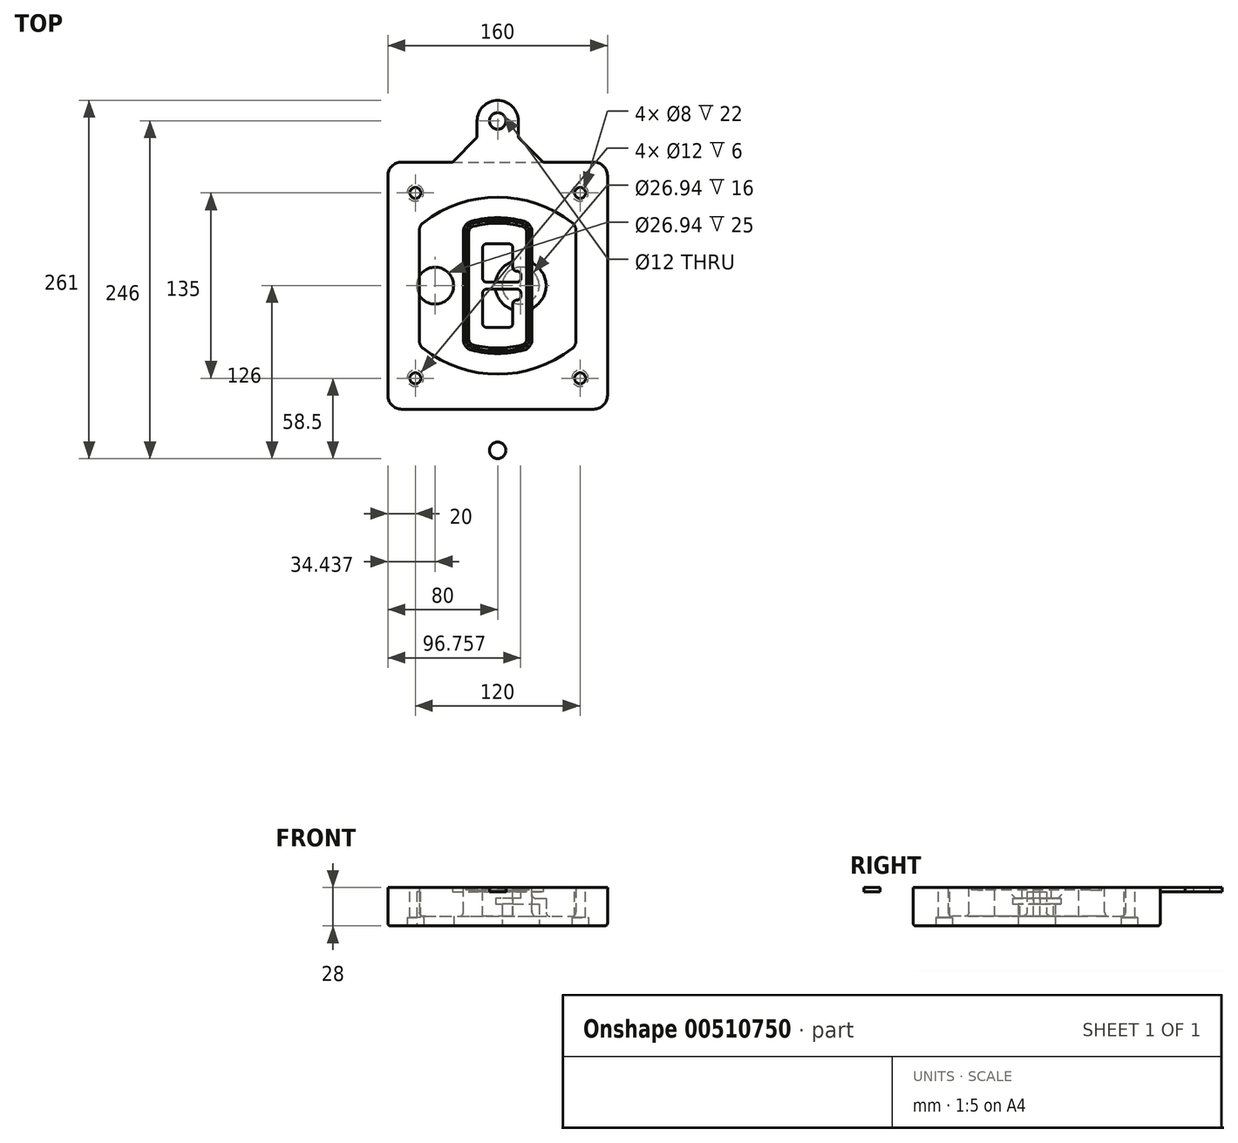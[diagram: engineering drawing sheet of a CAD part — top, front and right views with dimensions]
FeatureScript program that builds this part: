
annotation { "Feature Type Name" : "Feature", "Feature Type Description" : "" }
export const myFeature = defineFeature(function(context is Context, id is Id, definition is map)
    precondition{}
    {
        {
            var Q0;
            Q0=qCreatedBy(makeId("Top.planeOp"),FACE);
            var sketch = newSketch(context, id + "F0", { "sketchPlane" : qUnion([Q0])});
            skPoint(sketch, "E0.rect.middle", {"position": v(0, 0) * mm});
            skLineSegment(sketch, "E1.bottom", {"start": v(-70, -90) * mm, "end": v(70, -90) * mm});
            skLineSegment(sketch, "E1.top", {"start": v(-70, 90) * mm, "end": v(70, 90) * mm});
            skLineSegment(sketch, "E1.left", {"start": v(-80, -80) * mm, "end": v(-80, 80) * mm});
            skLineSegment(sketch, "E1.right", {"start": v(80, -80) * mm, "end": v(80, 80) * mm});
            skLineSegment(sketch, "E2", {"start": v(-80, 90) * mm, "end": v(80, -90) * mm, "construction": true});
            skLineSegment(sketch, "E3", {"start": v(80, 90) * mm, "end": v(-80, -90) * mm, "construction": true});
            skCircle(sketch, "E4", {"center": v(-60, 67.5) * mm, "radius": 4 * mm});
            skCircle(sketch, "E5", {"center": v(60, 67.5) * mm, "radius": 4 * mm});
            skCircle(sketch, "E6", {"center": v(60, -67.5) * mm, "radius": 4 * mm});
            skCircle(sketch, "E7", {"center": v(-60, -67.5) * mm, "radius": 4 * mm});
            skLineSegment(sketch, "E8", {"start": v(-60, 67.5) * mm, "end": v(60, 67.5) * mm, "construction": true});
            skLineSegment(sketch, "E9", {"start": v(60, 67.5) * mm, "end": v(60, -67.5) * mm, "construction": true});
            skLineSegment(sketch, "E10", {"start": v(60, -67.5) * mm, "end": v(-60, -67.5) * mm, "construction": true});
            skLineSegment(sketch, "E11", {"start": v(-60, -67.5) * mm, "end": v(-60, 67.5) * mm, "construction": true});
            skLineSegment(sketch, "E12", {"start": v(-60, 40.3) * mm, "end": v(-60, -40.3) * mm});
            skLineSegment(sketch, "E13", {"start": v(60, 40.3) * mm, "end": v(60, -40.3) * mm});
            skArc(sketch, "E14", {"start": v(56.15, 48.18) * mm, "mid": v(0, 67.5) * mm, "end": v(-56.15, 48.18) * mm});
            skArc(sketch, "E15", {"start": v(-56.15, -48.18) * mm, "mid": v(0, -67.5) * mm, "end": v(56.15, -48.18) * mm});
            skLineSegment(sketch, "E16", {"start": v(-60, 0) * mm, "end": v(60, 0) * mm, "construction": true});
            skPoint(sketch, "E17.visualSharp", {"position": v(-60, -45) * mm});
            skArc(sketch, "E17.filletArc", {"start": v(-60, -40.3) * mm, "mid": v(-58.99, -44.68) * mm, "end": v(-56.15, -48.18) * mm});
            skPoint(sketch, "E18.visualSharp", {"position": v(-60, 45) * mm});
            skArc(sketch, "E18.filletArc", {"start": v(-56.15, 48.18) * mm, "mid": v(-58.99, 44.68) * mm, "end": v(-60, 40.3) * mm});
            skPoint(sketch, "E19.visualSharp", {"position": v(60, 45) * mm});
            skArc(sketch, "E19.filletArc", {"start": v(60, 40.3) * mm, "mid": v(58.99, 44.68) * mm, "end": v(56.15, 48.18) * mm});
            skPoint(sketch, "E20.visualSharp", {"position": v(60, -45) * mm});
            skArc(sketch, "E20.filletArc", {"start": v(56.15, -48.18) * mm, "mid": v(58.99, -44.68) * mm, "end": v(60, -40.3) * mm});
            skPoint(sketch, "E21.visualSharp", {"position": v(-80, 90) * mm});
            skArc(sketch, "E21.filletArc", {"start": v(-70, 90) * mm, "mid": v(-77.07, 87.07) * mm, "end": v(-80, 80) * mm});
            skPoint(sketch, "E22.visualSharp", {"position": v(80, 90) * mm});
            skArc(sketch, "E22.filletArc", {"start": v(80, 80) * mm, "mid": v(77.07, 87.07) * mm, "end": v(70, 90) * mm});
            skPoint(sketch, "E23.visualSharp", {"position": v(80, -90) * mm});
            skArc(sketch, "E23.filletArc", {"start": v(70, -90) * mm, "mid": v(77.07, -87.07) * mm, "end": v(80, -80) * mm});
            skPoint(sketch, "E24.visualSharp", {"position": v(-80, -90) * mm});
            skArc(sketch, "E24.filletArc", {"start": v(-80, -80) * mm, "mid": v(-77.07, -87.07) * mm, "end": v(-70, -90) * mm});
            skArc(sketch, "E25.0", {"start": v(57, 40.3) * mm, "mid": v(56.3, 43.36) * mm, "end": v(54.3, 45.81) * mm});
            skLineSegment(sketch, "E25.1", {"start": v(57, 40.3) * mm, "end": v(57, -40.3) * mm});
            skArc(sketch, "E25.2", {"start": v(54.3, -45.81) * mm, "mid": v(56.3, -43.36) * mm, "end": v(57, -40.3) * mm});
            skArc(sketch, "E25.3", {"start": v(-54.3, -45.81) * mm, "mid": v(0, -64.5) * mm, "end": v(54.3, -45.81) * mm});
            skArc(sketch, "E25.4", {"start": v(-57, -40.3) * mm, "mid": v(-56.3, -43.36) * mm, "end": v(-54.3, -45.81) * mm});
            skArc(sketch, "E25.5", {"start": v(54.3, 45.81) * mm, "mid": v(0, 64.5) * mm, "end": v(-54.3, 45.81) * mm});
            skLineSegment(sketch, "E25.6", {"start": v(-57, 40.3) * mm, "end": v(-57, -40.3) * mm});
            skArc(sketch, "E25.7", {"start": v(-54.3, 45.81) * mm, "mid": v(-56.3, 43.36) * mm, "end": v(-57, 40.3) * mm});
            skArc(sketch, "E26.0", {"start": v(-58.62, 51.33) * mm, "mid": v(-62.58, 46.43) * mm, "end": v(-64, 40.3) * mm});
            skArc(sketch, "E26.1", {"start": v(58.62, 51.33) * mm, "mid": v(0, 71.5) * mm, "end": v(-58.62, 51.33) * mm});
            skArc(sketch, "E26.2", {"start": v(64, 40.3) * mm, "mid": v(62.58, 46.43) * mm, "end": v(58.62, 51.33) * mm});
            skLineSegment(sketch, "E26.3", {"start": v(64, 40.3) * mm, "end": v(64, -40.3) * mm});
            skArc(sketch, "E26.4", {"start": v(58.62, -51.33) * mm, "mid": v(62.58, -46.43) * mm, "end": v(64, -40.3) * mm});
            skLineSegment(sketch, "E26.5", {"start": v(-64, 40.3) * mm, "end": v(-64, -40.3) * mm});
            skArc(sketch, "E26.6", {"start": v(-58.62, -51.33) * mm, "mid": v(0, -71.5) * mm, "end": v(58.62, -51.33) * mm});
            skArc(sketch, "E26.7", {"start": v(-64, -40.3) * mm, "mid": v(-62.58, -46.43) * mm, "end": v(-58.62, -51.33) * mm});
            skSolve(sketch);
        }
        {
            var Q0;
            Q0=makeQuery(id+"F0.imprint","IMPRINT",FACE,{"disambiguationData":[TD([[makeQuery(id+"F0.imprint","IMPRINT",EDGE,{"derivedFrom":sQuery(id+"F0.wireOp",EDGE,"E1.bottom")}),1.0]])]});
            var Q1;
            Q1=makeQuery(id+"F0.imprint","IMPRINT",FACE,{"disambiguationData":[TD([[makeQuery(id+"F0.imprint","IMPRINT",EDGE,{"derivedFrom":sQuery(id+"F0.wireOp",EDGE,"E12")}),1.0]])]});
            var Q2;
            Q2=makeQuery(id+"F0.imprint","IMPRINT",FACE,{"disambiguationData":[TD([[makeQuery(id+"F0.imprint","IMPRINT",EDGE,{"derivedFrom":sQuery(id+"F0.wireOp",EDGE,"E25.0")}),1.0]])]});
            var Q3;
            Q3=makeQuery(id+"F0.imprint","IMPRINT",FACE,{"disambiguationData":[TD([[makeQuery(id+"F0.imprint","IMPRINT",EDGE,{"derivedFrom":sQuery(id+"F0.wireOp",EDGE,"E12")}),-1.0]])]});
            extrude(context, id + "F1", {"entities" : qUnion([Q0, Q1, Q2, Q3]), "oppositeDirection" : true, "depth" : 25 * mm});
        }
        {
            var Q0;
            Q0=makeQuery(id+"F0.imprint","IMPRINT",FACE,{"disambiguationData":[TD([[makeQuery(id+"F0.imprint","IMPRINT",EDGE,{"derivedFrom":sQuery(id+"F0.wireOp",EDGE,"E12")}),1.0]])]});
            extrude(context, id + "F2", {"entities" : qUnion([Q0]), "operationType" : NewBodyOperationType.ADD, "depth" : 3 * mm});
        }
        {
            var Q0;
            Q0=makeQuery(id+"F0.imprint","IMPRINT",FACE,{"disambiguationData":[TD([[makeQuery(id+"F0.imprint","IMPRINT",EDGE,{"derivedFrom":sQuery(id+"F0.wireOp",EDGE,"E25.0")}),1.0]])]});
            extrude(context, id + "F3", {"entities" : qUnion([Q0]), "operationType" : NewBodyOperationType.REMOVE, "oppositeDirection" : true, "depth" : 18 * mm});
        }
        {
            var Q0;
            Q0=makeQuery(id+"F2.opExtrude","CAP_FACE",FACE,{"disambiguationData":[OSD([sQuery(id+"F0.wireOp",EDGE,"E12"),sQuery(id+"F0.wireOp",EDGE,"E13"),sQuery(id+"F0.wireOp",EDGE,"E14"),sQuery(id+"F0.wireOp",EDGE,"E15"),sQuery(id+"F0.wireOp",EDGE,"E17.filletArc"),sQuery(id+"F0.wireOp",EDGE,"E18.filletArc"),sQuery(id+"F0.wireOp",EDGE,"E19.filletArc"),sQuery(id+"F0.wireOp",EDGE,"E20.filletArc"),sQuery(id+"F0.wireOp",EDGE,"E25.0"),sQuery(id+"F0.wireOp",EDGE,"E25.1"),sQuery(id+"F0.wireOp",EDGE,"E25.2"),sQuery(id+"F0.wireOp",EDGE,"E25.3"),sQuery(id+"F0.wireOp",EDGE,"E25.4"),sQuery(id+"F0.wireOp",EDGE,"E25.5"),sQuery(id+"F0.wireOp",EDGE,"E25.6"),sQuery(id+"F0.wireOp",EDGE,"E25.7")])],"isStart":false});
            var sketch = newSketch(context, id + "F4", { "sketchPlane" : qUnion([Q0])});
            skArc(sketch, "E27.0", {"start": v(-19.08, -46.97) * mm, "mid": v(0, -49.5) * mm, "end": v(19.08, -46.97) * mm});
            skArc(sketch, "E28.0", {"start": v(19.08, 46.97) * mm, "mid": v(0, 49.5) * mm, "end": v(-19.08, 46.97) * mm});
            skLineSegment(sketch, "E29", {"start": v(-25, 39.25) * mm, "end": v(-25, -39.25) * mm});
            skLineSegment(sketch, "E30", {"start": v(25, 39.25) * mm, "end": v(25, -39.25) * mm});
            skLineSegment(sketch, "E31", {"start": v(-25, 45.1) * mm, "end": v(25, 45.1) * mm, "construction": true});
            skLineSegment(sketch, "E32", {"start": v(-25, -45.1) * mm, "end": v(25, -45.1) * mm, "construction": true});
            skPoint(sketch, "E33.visualSharp", {"position": v(-25, 45.1) * mm});
            skArc(sketch, "E33.filletArc", {"start": v(-19.08, 46.97) * mm, "mid": v(-23.35, 44.11) * mm, "end": v(-25, 39.25) * mm});
            skPoint(sketch, "E34.visualSharp", {"position": v(25, 45.1) * mm});
            skArc(sketch, "E34.filletArc", {"start": v(25, 39.25) * mm, "mid": v(23.35, 44.11) * mm, "end": v(19.08, 46.97) * mm});
            skPoint(sketch, "E35.visualSharp", {"position": v(25, -45.1) * mm});
            skArc(sketch, "E35.filletArc", {"start": v(19.08, -46.97) * mm, "mid": v(23.35, -44.11) * mm, "end": v(25, -39.25) * mm});
            skPoint(sketch, "E36.visualSharp", {"position": v(-25, -45.1) * mm});
            skArc(sketch, "E36.filletArc", {"start": v(-25, -39.25) * mm, "mid": v(-23.35, -44.11) * mm, "end": v(-19.08, -46.97) * mm});
            skArc(sketch, "E37.0", {"start": v(54.3, 45.81) * mm, "mid": v(0, 64.5) * mm, "end": v(-54.3, 45.81) * mm});
            skArc(sketch, "E37.1", {"start": v(-54.3, 45.81) * mm, "mid": v(-56.3, 43.36) * mm, "end": v(-57, 40.3) * mm});
            skLineSegment(sketch, "E37.2", {"start": v(-57, 40.3) * mm, "end": v(-57, -40.3) * mm});
            skArc(sketch, "E37.3", {"start": v(-57, -40.3) * mm, "mid": v(-56.3, -43.36) * mm, "end": v(-54.3, -45.81) * mm});
            skArc(sketch, "E37.4", {"start": v(-54.3, -45.81) * mm, "mid": v(0, -64.5) * mm, "end": v(54.3, -45.81) * mm});
            skArc(sketch, "E37.5", {"start": v(54.3, -45.81) * mm, "mid": v(56.3, -43.36) * mm, "end": v(57, -40.3) * mm});
            skLineSegment(sketch, "E37.6", {"start": v(57, 40.3) * mm, "end": v(57, -40.3) * mm});
            skArc(sketch, "E37.7", {"start": v(57, 40.3) * mm, "mid": v(56.3, 43.36) * mm, "end": v(54.3, 45.81) * mm});
            skLineSegment(sketch, "E38.0", {"start": v(23, 39.25) * mm, "end": v(23, -39.25) * mm});
            skArc(sketch, "E38.1", {"start": v(18.56, -45.04) * mm, "mid": v(21.76, -42.9) * mm, "end": v(23, -39.25) * mm});
            skArc(sketch, "E38.2", {"start": v(-18.56, -45.04) * mm, "mid": v(0, -47.5) * mm, "end": v(18.56, -45.04) * mm});
            skArc(sketch, "E38.3", {"start": v(-23, -39.25) * mm, "mid": v(-21.76, -42.9) * mm, "end": v(-18.56, -45.04) * mm});
            skLineSegment(sketch, "E38.4", {"start": v(-23, 39.25) * mm, "end": v(-23, -39.25) * mm});
            skArc(sketch, "E38.5", {"start": v(23, 39.25) * mm, "mid": v(21.76, 42.9) * mm, "end": v(18.56, 45.04) * mm});
            skArc(sketch, "E38.6", {"start": v(-18.56, 45.04) * mm, "mid": v(-21.76, 42.9) * mm, "end": v(-23, 39.25) * mm});
            skArc(sketch, "E38.7", {"start": v(18.56, 45.04) * mm, "mid": v(0, 47.5) * mm, "end": v(-18.56, 45.04) * mm});
            skArc(sketch, "E39.0", {"start": v(21, 39.25) * mm, "mid": v(20.18, 41.68) * mm, "end": v(18.04, 43.1) * mm});
            skLineSegment(sketch, "E39.1", {"start": v(21, 39.25) * mm, "end": v(21, -39.25) * mm});
            skArc(sketch, "E39.2", {"start": v(18.04, -43.1) * mm, "mid": v(20.18, -41.68) * mm, "end": v(21, -39.25) * mm});
            skArc(sketch, "E39.3", {"start": v(-18.04, -43.1) * mm, "mid": v(0, -45.5) * mm, "end": v(18.04, -43.1) * mm});
            skArc(sketch, "E39.4", {"start": v(-21, -39.25) * mm, "mid": v(-20.18, -41.68) * mm, "end": v(-18.04, -43.1) * mm});
            skArc(sketch, "E39.5", {"start": v(18.04, 43.1) * mm, "mid": v(0, 45.5) * mm, "end": v(-18.04, 43.1) * mm});
            skLineSegment(sketch, "E39.6", {"start": v(-21, 39.25) * mm, "end": v(-21, -39.25) * mm});
            skArc(sketch, "E39.7", {"start": v(-18.04, 43.1) * mm, "mid": v(-20.18, 41.68) * mm, "end": v(-21, 39.25) * mm});
            skLineSegment(sketch, "E40", {"start": v(-25, 0) * mm, "end": v(25, 0) * mm, "construction": true});
            skLineSegment(sketch, "E41", {"start": v(-11, 5.5) * mm, "end": v(-11, 27.5) * mm});
            skLineSegment(sketch, "E42", {"start": v(-8, 30.5) * mm, "end": v(8, 30.5) * mm});
            skLineSegment(sketch, "E43", {"start": v(11, 27.5) * mm, "end": v(11, 13.5) * mm});
            skLineSegment(sketch, "E44", {"start": v(14, 10.5) * mm, "end": v(14, 10.5) * mm});
            skLineSegment(sketch, "E45", {"start": v(17, 7.5) * mm, "end": v(17, 5.5) * mm});
            skLineSegment(sketch, "E46", {"start": v(14, 2.5) * mm, "end": v(-8, 2.5) * mm});
            skPoint(sketch, "E47.visualSharp", {"position": v(-11, 30.5) * mm});
            skArc(sketch, "E47.filletArc", {"start": v(-8, 30.5) * mm, "mid": v(-10.12, 29.62) * mm, "end": v(-11, 27.5) * mm});
            skPoint(sketch, "E48.visualSharp", {"position": v(11, 30.5) * mm});
            skArc(sketch, "E48.filletArc", {"start": v(11, 27.5) * mm, "mid": v(10.12, 29.62) * mm, "end": v(8, 30.5) * mm});
            skPoint(sketch, "E49.visualSharp", {"position": v(11, 10.5) * mm});
            skArc(sketch, "E49.filletArc", {"start": v(11, 13.5) * mm, "mid": v(11.88, 11.38) * mm, "end": v(14, 10.5) * mm});
            skPoint(sketch, "E50.visualSharp", {"position": v(17, 10.5) * mm});
            skArc(sketch, "E50.filletArc", {"start": v(17, 7.5) * mm, "mid": v(16.12, 9.62) * mm, "end": v(14, 10.5) * mm});
            skPoint(sketch, "E51.visualSharp", {"position": v(17, 2.5) * mm});
            skArc(sketch, "E51.filletArc", {"start": v(14, 2.5) * mm, "mid": v(16.12, 3.38) * mm, "end": v(17, 5.5) * mm});
            skPoint(sketch, "E52.visualSharp", {"position": v(-11, 2.5) * mm});
            skArc(sketch, "E52.filletArc", {"start": v(-11, 5.5) * mm, "mid": v(-10.12, 3.38) * mm, "end": v(-8, 2.5) * mm});
            skLineSegment(sketch, "E53.0.MirrorCS", {"start": v(14, -2.5) * mm, "end": v(-8, -2.5) * mm});
            skArc(sketch, "E54.0.MirrorCS", {"start": v(-11, -5.5) * mm, "mid": v(-10.12, -3.38) * mm, "end": v(-8, -2.5) * mm});
            skLineSegment(sketch, "E55.0.MirrorCS", {"start": v(-11, -5.5) * mm, "end": v(-11, -27.5) * mm});
            skArc(sketch, "E56.0.MirrorCS", {"start": v(-8, -30.5) * mm, "mid": v(-10.12, -29.62) * mm, "end": v(-11, -27.5) * mm});
            skLineSegment(sketch, "E57.0.MirrorCS", {"start": v(-8, -30.5) * mm, "end": v(8, -30.5) * mm});
            skArc(sketch, "E58.0.MirrorCS", {"start": v(11, -27.5) * mm, "mid": v(10.12, -29.62) * mm, "end": v(8, -30.5) * mm});
            skLineSegment(sketch, "E59.0.MirrorCS", {"start": v(11, -27.5) * mm, "end": v(11, -13.5) * mm});
            skArc(sketch, "E60.0.MirrorCS", {"start": v(11, -13.5) * mm, "mid": v(11.88, -11.38) * mm, "end": v(14, -10.5) * mm});
            skArc(sketch, "E61.0.MirrorCS", {"start": v(17, -7.5) * mm, "mid": v(16.12, -9.62) * mm, "end": v(14, -10.5) * mm});
            skLineSegment(sketch, "E62.0.MirrorCS", {"start": v(17, -7.5) * mm, "end": v(17, -5.5) * mm});
            skArc(sketch, "E63.0.MirrorCS", {"start": v(14, -2.5) * mm, "mid": v(16.12, -3.38) * mm, "end": v(17, -5.5) * mm});
            skSolve(sketch);
        }
        {
            var Q0;
            Q0=makeQuery(id+"F4.imprint","IMPRINT",FACE,{"disambiguationData":[TD([[makeQuery(id+"F4.imprint","IMPRINT",EDGE,{"derivedFrom":sQuery(id+"F4.wireOp",EDGE,"E27.0")}),1.0]])]});
            var Q1;
            Q1=makeQuery(id+"F4.imprint","IMPRINT",FACE,{"disambiguationData":[TD([[makeQuery(id+"F4.imprint","IMPRINT",EDGE,{"derivedFrom":sQuery(id+"F4.wireOp",EDGE,"E38.0")}),-1.0]])]});
            var Q2;
            Q2=makeQuery(id+"F4.imprint","IMPRINT",FACE,{"disambiguationData":[TD([[makeQuery(id+"F4.imprint","IMPRINT",EDGE,{"derivedFrom":sQuery(id+"F4.wireOp",EDGE,"E39.0")}),1.0]])]});
            extrude(context, id + "F5", {"entities" : qUnion([Q0, Q1, Q2]), "operationType" : NewBodyOperationType.ADD, "endBound" : BoundingType.UP_TO_NEXT, "oppositeDirection" : true, "depth" : 25 * mm});
        }
        {
            var Q0;
            Q0=makeQuery(id+"F4.imprint","IMPRINT",FACE,{"disambiguationData":[TD([[makeQuery(id+"F4.imprint","IMPRINT",EDGE,{"derivedFrom":sQuery(id+"F4.wireOp",EDGE,"E38.0")}),-1.0]])]});
            extrude(context, id + "F6", {"entities" : qUnion([Q0]), "operationType" : NewBodyOperationType.REMOVE, "oppositeDirection" : true, "depth" : 2 * mm});
        }
        {
            var Q0;
            Q0=makeQuery(id+"F1.opExtrude","CAP_FACE",FACE,{"disambiguationData":[OSD([sQuery(id+"F0.wireOp",EDGE,"E1.bottom"),sQuery(id+"F0.wireOp",EDGE,"E1.top"),sQuery(id+"F0.wireOp",EDGE,"E1.left"),sQuery(id+"F0.wireOp",EDGE,"E1.right"),sQuery(id+"F0.wireOp",EDGE,"E4"),sQuery(id+"F0.wireOp",EDGE,"E5"),sQuery(id+"F0.wireOp",EDGE,"E6"),sQuery(id+"F0.wireOp",EDGE,"E7"),sQuery(id+"F0.wireOp",EDGE,"E21.filletArc"),sQuery(id+"F0.wireOp",EDGE,"E22.filletArc"),sQuery(id+"F0.wireOp",EDGE,"E23.filletArc"),sQuery(id+"F0.wireOp",EDGE,"E24.filletArc")])],"isStart":false});
            var sketch = newSketch(context, id + "F7", { "sketchPlane" : qUnion([Q0])});
            skCircle(sketch, "E64", {"center": v(16.76, 0) * mm, "radius": 13.47 * mm});
            skCircle(sketch, "E65", {"center": v(-45.56, 0) * mm, "radius": 13.47 * mm});
            skLineSegment(sketch, "E66", {"start": v(80, 0) * mm, "end": v(-80, 0) * mm});
            skCircle(sketch, "E67", {"center": v(16.76, 0) * mm, "radius": 18.47 * mm});
            skCircle(sketch, "E68", {"center": v(60, -67.5) * mm, "radius": 6 * mm});
            skCircle(sketch, "E69", {"center": v(-60, -67.5) * mm, "radius": 6 * mm});
            skCircle(sketch, "E70", {"center": v(-60, 67.5) * mm, "radius": 6 * mm});
            skCircle(sketch, "E71", {"center": v(60, 67.5) * mm, "radius": 6 * mm});
            skSolve(sketch);
        }
        {
            var Q0;
            {var subQ1=sQuery(id+"F7.wireOp",EDGE,"E66");var subQ4=sQuery(id+"F7.wireOp",EDGE,"E64");var subQ6=makeQuery(id+"F7.imprint","INTERSECT",VERTEX,{"disambiguationData":[OD(0.0)],"derivedFrom":[subQ4,subQ1]});Q0=makeQuery(id+"F7.imprint","IMPRINT",FACE,{"disambiguationData":[TD([[makeQuery(id+"F7.imprint","IMPRINT",EDGE,{"disambiguationData":[TD([[subQ6,-1.0]])],"derivedFrom":subQ4}),-1.0]])]});}
            var Q1;
            {var subQ0=sQuery(id+"F7.wireOp",EDGE,"E66");var subQ1=sQuery(id+"F7.wireOp",EDGE,"E64");var subQ3=makeQuery(id+"F7.imprint","INTERSECT",VERTEX,{"disambiguationData":[OD(0.0)],"derivedFrom":[subQ1,subQ0]});Q1=makeQuery(id+"F7.imprint","IMPRINT",FACE,{"disambiguationData":[TD([[makeQuery(id+"F7.imprint","IMPRINT",EDGE,{"disambiguationData":[TD([[subQ3,-1.0]])],"derivedFrom":subQ1}),1.0]])]});}
            var Q2;
            {var subQ0=sQuery(id+"F7.wireOp",EDGE,"E66");var subQ1=sQuery(id+"F7.wireOp",EDGE,"E64");var subQ3=makeQuery(id+"F7.imprint","INTERSECT",VERTEX,{"disambiguationData":[OD(0.0)],"derivedFrom":[subQ1,subQ0]});Q2=makeQuery(id+"F7.imprint","IMPRINT",FACE,{"disambiguationData":[TD([[makeQuery(id+"F7.imprint","IMPRINT",EDGE,{"disambiguationData":[TD([[subQ3,1.0]])],"derivedFrom":subQ1}),1.0]])]});}
            var Q3;
            {var subQ1=sQuery(id+"F7.wireOp",EDGE,"E66");var subQ4=sQuery(id+"F7.wireOp",EDGE,"E64");var subQ6=makeQuery(id+"F7.imprint","INTERSECT",VERTEX,{"disambiguationData":[OD(0.0)],"derivedFrom":[subQ4,subQ1]});Q3=makeQuery(id+"F7.imprint","IMPRINT",FACE,{"disambiguationData":[TD([[makeQuery(id+"F7.imprint","IMPRINT",EDGE,{"disambiguationData":[TD([[subQ6,1.0]])],"derivedFrom":subQ4}),-1.0]])]});}
            extrude(context, id + "F8", {"entities" : qUnion([Q0, Q1, Q2, Q3]), "operationType" : NewBodyOperationType.ADD, "oppositeDirection" : true, "depth" : 20 * mm});
        }
        {
            var Q0;
            {var subQ0=sQuery(id+"F7.wireOp",EDGE,"E66");var subQ1=sQuery(id+"F7.wireOp",EDGE,"E64");var subQ3=makeQuery(id+"F7.imprint","INTERSECT",VERTEX,{"disambiguationData":[OD(0.0)],"derivedFrom":[subQ1,subQ0]});Q0=makeQuery(id+"F7.imprint","IMPRINT",FACE,{"disambiguationData":[TD([[makeQuery(id+"F7.imprint","IMPRINT",EDGE,{"disambiguationData":[TD([[subQ3,-1.0]])],"derivedFrom":subQ1}),1.0]])]});}
            var Q1;
            {var subQ0=sQuery(id+"F7.wireOp",EDGE,"E66");var subQ1=sQuery(id+"F7.wireOp",EDGE,"E64");var subQ3=makeQuery(id+"F7.imprint","INTERSECT",VERTEX,{"disambiguationData":[OD(0.0)],"derivedFrom":[subQ1,subQ0]});Q1=makeQuery(id+"F7.imprint","IMPRINT",FACE,{"disambiguationData":[TD([[makeQuery(id+"F7.imprint","IMPRINT",EDGE,{"disambiguationData":[TD([[subQ3,1.0]])],"derivedFrom":subQ1}),1.0]])]});}
            extrude(context, id + "F9", {"entities" : qUnion([Q0, Q1]), "operationType" : NewBodyOperationType.REMOVE, "oppositeDirection" : true, "depth" : 16 * mm});
        }
        {
            var Q0;
            {var subQ0=sQuery(id+"F7.wireOp",EDGE,"E66");var subQ1=sQuery(id+"F7.wireOp",EDGE,"E65");var subQ3=makeQuery(id+"F7.imprint","INTERSECT",VERTEX,{"disambiguationData":[OD(0.0)],"derivedFrom":[subQ1,subQ0]});Q0=makeQuery(id+"F7.imprint","IMPRINT",FACE,{"disambiguationData":[TD([[makeQuery(id+"F7.imprint","IMPRINT",EDGE,{"disambiguationData":[TD([[subQ3,-1.0]])],"derivedFrom":subQ1}),1.0]])]});}
            var Q1;
            {var subQ0=sQuery(id+"F7.wireOp",EDGE,"E66");var subQ1=sQuery(id+"F7.wireOp",EDGE,"E65");var subQ3=makeQuery(id+"F7.imprint","INTERSECT",VERTEX,{"disambiguationData":[OD(0.0)],"derivedFrom":[subQ1,subQ0]});Q1=makeQuery(id+"F7.imprint","IMPRINT",FACE,{"disambiguationData":[TD([[makeQuery(id+"F7.imprint","IMPRINT",EDGE,{"disambiguationData":[TD([[subQ3,1.0]])],"derivedFrom":subQ1}),1.0]])]});}
            extrude(context, id + "F10", {"entities" : qUnion([Q0, Q1]), "operationType" : NewBodyOperationType.REMOVE, "oppositeDirection" : true, "depth" : 25 * mm});
        }
        {
            var Q0;
            Q0=makeQuery(id+"F7.imprint","IMPRINT",FACE,{"disambiguationData":[TD([[makeQuery(id+"F7.imprint","IMPRINT",EDGE,{"derivedFrom":sQuery(id+"F7.wireOp",EDGE,"E68")}),1.0]])]});
            var Q1;
            Q1=makeQuery(id+"F7.imprint","IMPRINT",FACE,{"disambiguationData":[TD([[makeQuery(id+"F7.imprint","IMPRINT",EDGE,{"derivedFrom":makeQuery(id+"F1.opExtrude","CAP_EDGE",EDGE,{"disambiguationData":[OSD([sQuery(id+"F0.wireOp",EDGE,"E5")])],"isStart":false})}),-1.0]])]});
            var Q2;
            Q2=makeQuery(id+"F7.imprint","IMPRINT",FACE,{"disambiguationData":[TD([[makeQuery(id+"F7.imprint","IMPRINT",EDGE,{"derivedFrom":sQuery(id+"F7.wireOp",EDGE,"E69")}),1.0]])]});
            var Q3;
            Q3=makeQuery(id+"F7.imprint","IMPRINT",FACE,{"disambiguationData":[TD([[makeQuery(id+"F7.imprint","IMPRINT",EDGE,{"derivedFrom":makeQuery(id+"F1.opExtrude","CAP_EDGE",EDGE,{"disambiguationData":[OSD([sQuery(id+"F0.wireOp",EDGE,"E4")])],"isStart":false})}),-1.0]])]});
            var Q4;
            Q4=makeQuery(id+"F7.imprint","IMPRINT",FACE,{"disambiguationData":[TD([[makeQuery(id+"F7.imprint","IMPRINT",EDGE,{"derivedFrom":sQuery(id+"F7.wireOp",EDGE,"E70")}),1.0]])]});
            var Q5;
            Q5=makeQuery(id+"F7.imprint","IMPRINT",FACE,{"disambiguationData":[TD([[makeQuery(id+"F7.imprint","IMPRINT",EDGE,{"derivedFrom":makeQuery(id+"F1.opExtrude","CAP_EDGE",EDGE,{"disambiguationData":[OSD([sQuery(id+"F0.wireOp",EDGE,"E7")])],"isStart":false})}),-1.0]])]});
            var Q6;
            Q6=makeQuery(id+"F7.imprint","IMPRINT",FACE,{"disambiguationData":[TD([[makeQuery(id+"F7.imprint","IMPRINT",EDGE,{"derivedFrom":sQuery(id+"F7.wireOp",EDGE,"E71")}),1.0]])]});
            var Q7;
            Q7=makeQuery(id+"F7.imprint","IMPRINT",FACE,{"disambiguationData":[TD([[makeQuery(id+"F7.imprint","IMPRINT",EDGE,{"derivedFrom":makeQuery(id+"F1.opExtrude","CAP_EDGE",EDGE,{"disambiguationData":[OSD([sQuery(id+"F0.wireOp",EDGE,"E6")])],"isStart":false})}),-1.0]])]});
            extrude(context, id + "F11", {"entities" : qUnion([Q0, Q1, Q2, Q3, Q4, Q5, Q6, Q7]), "operationType" : NewBodyOperationType.REMOVE, "oppositeDirection" : true, "depth" : 6 * mm});
        }
        {
            var Q0;
            Q0=makeQuery(id+"F9.boolean.opBoolean","COPY",FACE,{"derivedFrom":makeQuery(id+"F9.opExtrude","CAP_FACE",FACE,{"disambiguationData":[OSD([sQuery(id+"F7.wireOp",EDGE,"E64")])],"isStart":false})});
            var sketch = newSketch(context, id + "F12", { "sketchPlane" : qUnion([Q0])});
            skArc(sketch, "E72.0", {"start": v(11, 17.55) * mm, "mid": v(2.57, 11.82) * mm, "end": v(-1.54, 2.5) * mm});
            skArc(sketch, "E72.1", {"start": v(-1.54, -2.5) * mm, "mid": v(2.57, -11.82) * mm, "end": v(11, -17.55) * mm});
            skLineSegment(sketch, "E73", {"start": v(-1.54, -2.5) * mm, "end": v(14, -2.5) * mm});
            skLineSegment(sketch, "E74.0", {"start": v(14, 2.5) * mm, "end": v(-1.54, 2.5) * mm});
            skArc(sketch, "E74.1", {"start": v(14, 2.5) * mm, "mid": v(16.12, 3.38) * mm, "end": v(17, 5.5) * mm});
            skLineSegment(sketch, "E74.2", {"start": v(17, 7.5) * mm, "end": v(17, 5.5) * mm});
            skArc(sketch, "E74.3", {"start": v(17, 7.5) * mm, "mid": v(16.12, 9.62) * mm, "end": v(14, 10.5) * mm});
            skArc(sketch, "E74.4", {"start": v(11, 13.5) * mm, "mid": v(11.88, 11.38) * mm, "end": v(14, 10.5) * mm});
            skLineSegment(sketch, "E74.5", {"start": v(11, 17.55) * mm, "end": v(11, 13.5) * mm});
            skLineSegment(sketch, "E74.7", {"start": v(14, -2.5) * mm, "end": v(-1.54, -2.5) * mm});
            skArc(sketch, "E74.8", {"start": v(14, -2.5) * mm, "mid": v(16.12, -3.38) * mm, "end": v(17, -5.5) * mm});
            skLineSegment(sketch, "E74.9", {"start": v(17, -7.5) * mm, "end": v(17, -5.5) * mm});
            skArc(sketch, "E74.10", {"start": v(17, -7.5) * mm, "mid": v(16.12, -9.62) * mm, "end": v(14, -10.5) * mm});
            skArc(sketch, "E74.11", {"start": v(11, -13.5) * mm, "mid": v(11.88, -11.38) * mm, "end": v(14, -10.5) * mm});
            skLineSegment(sketch, "E74.12", {"start": v(11, -17.55) * mm, "end": v(11, -13.5) * mm});
            skPoint(sketch, "E75.orphan", {"position": v(11, -27.5) * mm});
            skPoint(sketch, "E76.orphan", {"position": v(-8, -2.5) * mm});
            skPoint(sketch, "E77.orphan", {"position": v(-8, 2.5) * mm});
            skPoint(sketch, "E78.orphan", {"position": v(11, 27.5) * mm});
            skSolve(sketch);
        }
        {
            var Q0;
            {var subQ7=sQuery(id+"F12.wireOp",EDGE,"E72.0");var subQ14=sQuery(id+"F12.wireOp",EDGE,"E72.1");var subQ16=sQuery(id+"F12.wireOp",EDGE,"E74.1");var subQ18=sQuery(id+"F12.wireOp",EDGE,"E74.8");Q0=qUnion([makeQuery(id+"F12.imprint","IMPRINT",FACE,{"disambiguationData":[TD([[makeQuery(id+"F12.imprint","IMPRINT",EDGE,{"derivedFrom":subQ7}),1.0]])]}),makeQuery(id+"F12.imprint","IMPRINT",FACE,{"disambiguationData":[TD([[makeQuery(id+"F12.imprint","IMPRINT",EDGE,{"derivedFrom":subQ14}),1.0]])]}),makeQuery(id+"F12.imprint","IMPRINT",FACE,{"disambiguationData":[TD([[makeQuery(id+"F12.imprint","IMPRINT",EDGE,{"derivedFrom":subQ16}),1.0]])]}),makeQuery(id+"F12.imprint","IMPRINT",FACE,{"disambiguationData":[TD([[makeQuery(id+"F12.imprint","IMPRINT",EDGE,{"derivedFrom":subQ18}),-1.0]])]})]);}
            var Q1;
            Q1=makeQuery(id+"F5.boolean.opBoolean","SPLIT",FACE,{"disambiguationData":[TD([makeQuery(id+"F5.opExtrude","SWEPT_FACE",FACE,{"disambiguationData":[OSD([sQuery(id+"F4.wireOp",EDGE,"E41")])]})])],"derivedFrom":makeQuery(id+"F3.boolean.opBoolean","COPY",FACE,{"derivedFrom":makeQuery(id+"F3.opExtrude","CAP_FACE",FACE,{"disambiguationData":[OSD([sQuery(id+"F0.wireOp",EDGE,"E25.0"),sQuery(id+"F0.wireOp",EDGE,"E25.1"),sQuery(id+"F0.wireOp",EDGE,"E25.2"),sQuery(id+"F0.wireOp",EDGE,"E25.3"),sQuery(id+"F0.wireOp",EDGE,"E25.4"),sQuery(id+"F0.wireOp",EDGE,"E25.5"),sQuery(id+"F0.wireOp",EDGE,"E25.6"),sQuery(id+"F0.wireOp",EDGE,"E25.7")])],"isStart":false})})});
            extrude(context, id + "F13", {"entities" : qUnion([Q0]), "operationType" : NewBodyOperationType.REMOVE, "endBound" : BoundingType.UP_TO_SURFACE, "endBoundEntityFace" : qUnion([Q1]), "depth" : 25 * mm});
        }
        {
            var Q0;
            Q0=makeQuery(id+"F3.boolean.opBoolean","COPY",EDGE,{"derivedFrom":makeQuery(id+"F3.opExtrude","CAP_EDGE",EDGE,{"disambiguationData":[OSD([sQuery(id+"F0.wireOp",EDGE,"E25.6")])],"isStart":false})});
            var Q1;
            Q1=makeQuery(id+"F8.boolean.opBoolean","INTERSECT",EDGE,{"derivedFrom":[makeQuery(id+"F5.opExtrude","SWEPT_FACE",FACE,{"disambiguationData":[OSD([sQuery(id+"F4.wireOp",EDGE,"E30")])]}),makeQuery(id+"F8.opExtrude","CAP_FACE",FACE,{"disambiguationData":[OSD([sQuery(id+"F7.wireOp",EDGE,"E67")])],"isStart":false})]});
            var Q2;
            Q2=makeQuery(id+"F8.boolean.opBoolean","INTERSECT",EDGE,{"disambiguationData":[OD(1.0)],"derivedFrom":[makeQuery(id+"F5.opExtrude","SWEPT_FACE",FACE,{"disambiguationData":[OSD([sQuery(id+"F4.wireOp",EDGE,"E30")])]}),makeQuery(id+"F8.opExtrude","SWEPT_FACE",FACE,{"disambiguationData":[OSD([sQuery(id+"F7.wireOp",EDGE,"E67")])]})]});
            var Q3;
            {var subQ0=sQuery(id+"F4.wireOp",EDGE,"E30");Q3=makeQuery(id+"F8.boolean.opBoolean","SPLIT",EDGE,{"disambiguationData":[TD([makeQuery(id+"F5.opExtrude","SWEPT_FACE",FACE,{"disambiguationData":[OSD([sQuery(id+"F4.wireOp",EDGE,"E35.filletArc")])]})])],"derivedFrom":makeQuery(id+"F5.opExtrude","CAP_EDGE",EDGE,{"disambiguationData":[OSD([subQ0])],"isStart":false})});}
            var Q4;
            {var subQ0=sQuery(id+"F0.wireOp",EDGE,"E25.7");var subQ1=sQuery(id+"F0.wireOp",EDGE,"E25.1");var subQ2=sQuery(id+"F0.wireOp",EDGE,"E25.6");var subQ3=sQuery(id+"F0.wireOp",EDGE,"E25.5");var subQ4=sQuery(id+"F0.wireOp",EDGE,"E25.4");var subQ5=sQuery(id+"F0.wireOp",EDGE,"E25.0");var subQ6=sQuery(id+"F0.wireOp",EDGE,"E25.2");var subQ7=sQuery(id+"F0.wireOp",EDGE,"E25.3");Q4=makeQuery(id+"F8.boolean.opBoolean","INTERSECT",EDGE,{"derivedFrom":[makeQuery(id+"F5.boolean.opBoolean","SPLIT",FACE,{"disambiguationData":[TD([makeQuery(id+"F2.opExtrude","SWEPT_FACE",FACE,{"disambiguationData":[OSD([subQ5])]})])],"derivedFrom":makeQuery(id+"F3.boolean.opBoolean","COPY",FACE,{"derivedFrom":makeQuery(id+"F3.opExtrude","CAP_FACE",FACE,{"disambiguationData":[OSD([subQ5,subQ1,subQ6,subQ7,subQ4,subQ3,subQ2,subQ0])],"isStart":false})})}),makeQuery(id+"F8.opExtrude","SWEPT_FACE",FACE,{"disambiguationData":[OSD([sQuery(id+"F7.wireOp",EDGE,"E67")])]})]});}
            var Q5;
            Q5=makeQuery(id+"F8.boolean.opBoolean","INTERSECT",EDGE,{"disambiguationData":[OD(0.0)],"derivedFrom":[makeQuery(id+"F5.opExtrude","SWEPT_FACE",FACE,{"disambiguationData":[OSD([sQuery(id+"F4.wireOp",EDGE,"E30")])]}),makeQuery(id+"F8.opExtrude","SWEPT_FACE",FACE,{"disambiguationData":[OSD([sQuery(id+"F7.wireOp",EDGE,"E67")])]})]});
            fillet(context, id + "F14", {"entities" : qUnion([Q0, Q1, Q2, Q3, Q4, Q5]), "radius" : 3 * mm, "tangentPropagation" : true, "allowEdgeOverflow" : false});
        }
        {
            var Q0;
            Q0=makeQuery(id+"F1.opExtrude","CAP_EDGE",EDGE,{"disambiguationData":[OSD([sQuery(id+"F0.wireOp",EDGE,"E1.bottom")])],"isStart":false});
            fillet(context, id + "F15", {"entities" : qUnion([Q0]), "radius" : 2 * mm, "tangentPropagation" : true, "allowEdgeOverflow" : false});
        }
        {
            var Q0;
            {var subQ0=sQuery(id+"F0.wireOp",EDGE,"E21.filletArc");var subQ1=sQuery(id+"F0.wireOp",EDGE,"E7");var subQ2=sQuery(id+"F0.wireOp",EDGE,"E6");var subQ3=sQuery(id+"F0.wireOp",EDGE,"E5");var subQ4=sQuery(id+"F0.wireOp",EDGE,"E4");var subQ5=sQuery(id+"F0.wireOp",EDGE,"E22.filletArc");var subQ6=sQuery(id+"F0.wireOp",EDGE,"E1.bottom");var subQ7=sQuery(id+"F0.wireOp",EDGE,"E1.right");var subQ8=sQuery(id+"F0.wireOp",EDGE,"E1.top");var subQ9=sQuery(id+"F0.wireOp",EDGE,"E1.left");var subQ10=sQuery(id+"F0.wireOp",EDGE,"E23.filletArc");var subQ11=sQuery(id+"F0.wireOp",EDGE,"E24.filletArc");Q0=makeQuery(id+"F2.boolean.opBoolean","SPLIT",FACE,{"disambiguationData":[TD([makeQuery(id+"F1.opExtrude","SWEPT_FACE",FACE,{"disambiguationData":[OSD([subQ6])]})])],"derivedFrom":makeQuery(id+"F1.opExtrude","CAP_FACE",FACE,{"disambiguationData":[OSD([subQ6,subQ8,subQ9,subQ7,subQ4,subQ3,subQ2,subQ1,subQ0,subQ5,subQ10,subQ11])],"isStart":true})});}
            var sketch = newSketch(context, id + "F16", { "sketchPlane" : qUnion([Q0])});
            skLineSegment(sketch, "E79", {"start": v(0, 90) * mm, "end": v(0, 120) * mm, "construction": true});
            skLineSegment(sketch, "E80", {"start": v(-33, 90) * mm, "end": v(-15, 108) * mm});
            skLineSegment(sketch, "E81", {"start": v(-15, 108) * mm, "end": v(-15, 120) * mm});
            skLineSegment(sketch, "E82", {"start": v(33, 90) * mm, "end": v(15, 108) * mm});
            skLineSegment(sketch, "E83", {"start": v(15, 108) * mm, "end": v(15, 120) * mm});
            skArc(sketch, "E84", {"start": v(15, 120) * mm, "mid": v(0, 135) * mm, "end": v(-15, 120) * mm});
            skCircle(sketch, "E85", {"center": v(0, 120) * mm, "radius": 6 * mm});
            skLineSegment(sketch, "E86", {"start": v(80, 0) * mm, "end": v(-80, 0) * mm, "construction": true});
            skCircle(sketch, "E87.MirrorC", {"center": v(0, -120) * mm, "radius": 6 * mm});
            skLineSegment(sketch, "E88.MirrorCS", {"start": v(0, -90) * mm, "end": v(0, -120) * mm, "construction": true});
            skLineSegment(sketch, "E89.MirrorCS", {"start": v(15, -108) * mm, "end": v(15, -120) * mm});
            skArc(sketch, "E90.MirrorCS", {"start": v(15, -120) * mm, "mid": v(0, -135) * mm, "end": v(-15, -120) * mm});
            skLineSegment(sketch, "E91.MirrorCS", {"start": v(-15, -108) * mm, "end": v(-15, -120) * mm});
            skLineSegment(sketch, "E92.MirrorCS", {"start": v(-33, -90) * mm, "end": v(-15, -108) * mm});
            skLineSegment(sketch, "E93.MirrorCS", {"start": v(33, -90) * mm, "end": v(15, -108) * mm});
            skSolve(sketch);
        }
        {
            var Q0;
            {var subQ0=sQuery(id+"F16.wireOp",EDGE,"E80");Q0=makeQuery(id+"F16.imprint","IMPRINT",FACE,{"disambiguationData":[TD([[makeQuery(id+"F16.imprint","IMPRINT",EDGE,{"derivedFrom":subQ0}),-1.0]])]});}
            var Q1;
            Q1=makeQuery(id+"F16.imprint","IMPRINT",FACE,{"disambiguationData":[TD([[makeQuery(id+"F16.imprint","IMPRINT",EDGE,{"derivedFrom":makeQuery(id+"F1.opExtrude","CAP_EDGE",EDGE,{"disambiguationData":[OSD([sQuery(id+"F0.wireOp",EDGE,"E1.left")])],"isStart":true})}),-1.0]])]});
            var Q2;
            Q2=makeQuery(id+"F16.imprint","IMPRINT",FACE,{"disambiguationData":[TD([[makeQuery(id+"F16.imprint","IMPRINT",EDGE,{"derivedFrom":sQuery(id+"F16.wireOp",EDGE,"E87.MirrorC")}),1.0]])]});
            var Q3;
            Q3=makeQuery(id+"F2.opExtrude","CAP_FACE",FACE,{"disambiguationData":[OSD([sQuery(id+"F0.wireOp",EDGE,"E12"),sQuery(id+"F0.wireOp",EDGE,"E13"),sQuery(id+"F0.wireOp",EDGE,"E14"),sQuery(id+"F0.wireOp",EDGE,"E15"),sQuery(id+"F0.wireOp",EDGE,"E17.filletArc"),sQuery(id+"F0.wireOp",EDGE,"E18.filletArc"),sQuery(id+"F0.wireOp",EDGE,"E19.filletArc"),sQuery(id+"F0.wireOp",EDGE,"E20.filletArc"),sQuery(id+"F0.wireOp",EDGE,"E25.0"),sQuery(id+"F0.wireOp",EDGE,"E25.1"),sQuery(id+"F0.wireOp",EDGE,"E25.2"),sQuery(id+"F0.wireOp",EDGE,"E25.3"),sQuery(id+"F0.wireOp",EDGE,"E25.4"),sQuery(id+"F0.wireOp",EDGE,"E25.5"),sQuery(id+"F0.wireOp",EDGE,"E25.6"),sQuery(id+"F0.wireOp",EDGE,"E25.7")])],"isStart":false});
            extrude(context, id + "F17", {"entities" : qUnion([Q0, Q1, Q2]), "operationType" : NewBodyOperationType.ADD, "endBound" : BoundingType.UP_TO_SURFACE, "endBoundEntityFace" : qUnion([Q3]), "depth" : 25 * mm});
        }
    });
